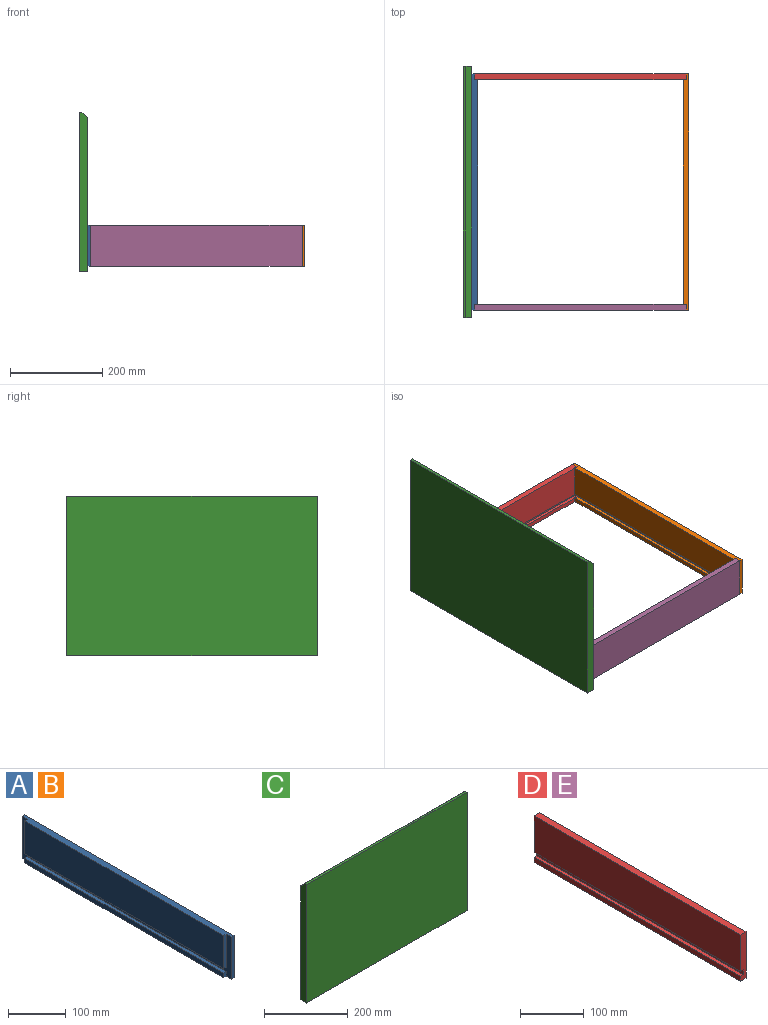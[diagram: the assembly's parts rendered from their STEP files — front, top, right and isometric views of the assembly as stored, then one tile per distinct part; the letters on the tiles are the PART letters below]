
ASSEMBLY  parts=5 mates=4
PART A: 14 faces, bbox 12.7x511.2x88.9 mm
  f0: plane 485.78x9.53mm, normal (-1,0,0), area 4627mm2, adj f6,f9,f10,f12
  f1: plane 69.85x6.35mm, normal (0,-1,0), area 443.5mm2, adj f3,f4,f11,f13
  f2: plane 69.85x6.35mm, normal (0,1,0), area 443.5mm2, adj f3,f4,f11,f13
  f3: plane 511.18x12.7mm, normal (0,0,1), area 6330.6mm2, adj f1,f2,f4,f5,f7,f8,f11
  f4: plane 485.78x69.85mm, normal (-1,0,0), area 33931.4mm2, adj f1,f2,f3,f13
  f5: plane 88.9x6.35mm, normal (0,-1,0), area 564.5mm2, adj f3,f6,f8,f11
  f6: plane 511.18x12.7mm, normal (0,0,-1), area 6330.6mm2, adj f0,f5,f7,f8,f9,f10,f11
  f7: plane 88.9x6.35mm, normal (0,1,0), area 564.5mm2, adj f3,f6,f8,f11
  f8: plane 511.18x88.9mm, normal (1,0,0), area 45443.5mm2, adj f3,f5,f6,f7
  f9: plane 9.53x6.35mm, normal (0,-1,0), area 60.5mm2, adj f0,f6,f11,f12
  f10: plane 9.53x6.35mm, normal (0,1,0), area 60.5mm2, adj f0,f6,f11,f12
  f11: plane 511.18x88.9mm, normal (-1,0,0), area 6885.1mm2, adj f1,f2,f3,f5,f6,f7,f9,f10
  f12: plane 485.78x6.35mm, normal (0,0,1), area 3084.7mm2, adj f0,f9,f10,f11
  f13: plane 485.78x6.35mm, normal (0,0,-1), area 3084.7mm2, adj f1,f2,f4,f11
PART B: same geometry as A
PART C: 7 faces, bbox 542.9x19.1x346.1 mm
  f0: plane 346.08x19.05mm, normal (-1,0,0), area 6512.1mm2, adj f1,f3,f4,f5,f6
  f1: plane 542.93x19.05mm, normal (0,0,-1), area 10342.7mm2, adj f0,f2,f4,f5
  f2: plane 346.08x19.05mm, normal (1,0,0), area 6512.1mm2, adj f1,f3,f4,f5,f6
  f3: plane 542.93x6.35mm, normal (0,0,1), area 3447.6mm2, adj f0,f2,f4,f6
  f4: plane 542.93x346.08mm, normal (0,-1,0), area 187892.8mm2, adj f0,f1,f2,f3
  f5: plane 542.93x333.38mm, normal (0,1,0), area 180997.6mm2, adj f0,f1,f2,f6
  f6: plane 542.93x12.7mm, normal (0,0.71,0.71), area 9751.2mm2, adj f0,f2,f3,f5
PART D: 10 faces, bbox 12.7x457.2x88.9 mm
  f0: plane 457.2x9.53mm, normal (-1,0,0), area 4354.8mm2, adj f1,f2,f3,f8
  f1: plane 88.9x12.7mm, normal (0,-1,0), area 1068.5mm2, adj f0,f2,f4,f5,f6,f7,f8,f9
  f2: plane 457.2x12.7mm, normal (0,0,-1), area 5806.4mm2, adj f0,f1,f3,f5
  f3: plane 88.9x12.7mm, normal (0,1,0), area 1068.5mm2, adj f0,f2,f4,f5,f6,f7,f8,f9
  f4: plane 457.2x12.7mm, normal (0,0,1), area 5806.4mm2, adj f1,f3,f5,f6
  f5: plane 457.2x88.9mm, normal (1,0,0), area 40645.1mm2, adj f1,f2,f3,f4
  f6: plane 457.2x69.85mm, normal (-1,0,0), area 31935.4mm2, adj f1,f3,f4,f7
  f7: plane 457.2x6.35mm, normal (0,0,-1), area 2903.2mm2, adj f1,f3,f6,f9
  f8: plane 457.2x6.35mm, normal (0,0,1), area 2903.2mm2, adj f0,f1,f3,f9
  f9: plane 457.2x9.53mm, normal (-1,0,0), area 4354.8mm2, adj f1,f3,f7,f8
PART E: same geometry as D
PLACE A rot(axis=(0,0,-1),180deg) t=(-330.3,257.51,182.53)mm
PLACE B t=(114.2,-253.67,182.53)mm
PLACE C rot(axis=(0,0,-1),90deg) t=(-343,273.38,169.83)mm
PLACE D rot(axis=(0,0,1),90deg) t=(120.55,244.81,182.53)mm
PLACE E rot(axis=(0,0,-1),90deg) t=(-336.65,-240.97,182.53)mm
MATE fastened B.f11 <-> D.f1  axis (-1,0,0) through (120.55,257.51,271.43)mm
MATE fastened A.f11 <-> D.f3  axis (1,0,0) through (-336.65,257.51,271.43)mm
MATE fastened E.f3 <-> B.f11  axis (1,0,0) through (120.55,-253.67,271.43)mm
MATE fastened C.f5 <-> A.f8  axis (1,0,0) through (-343,1.92,169.83)mm
